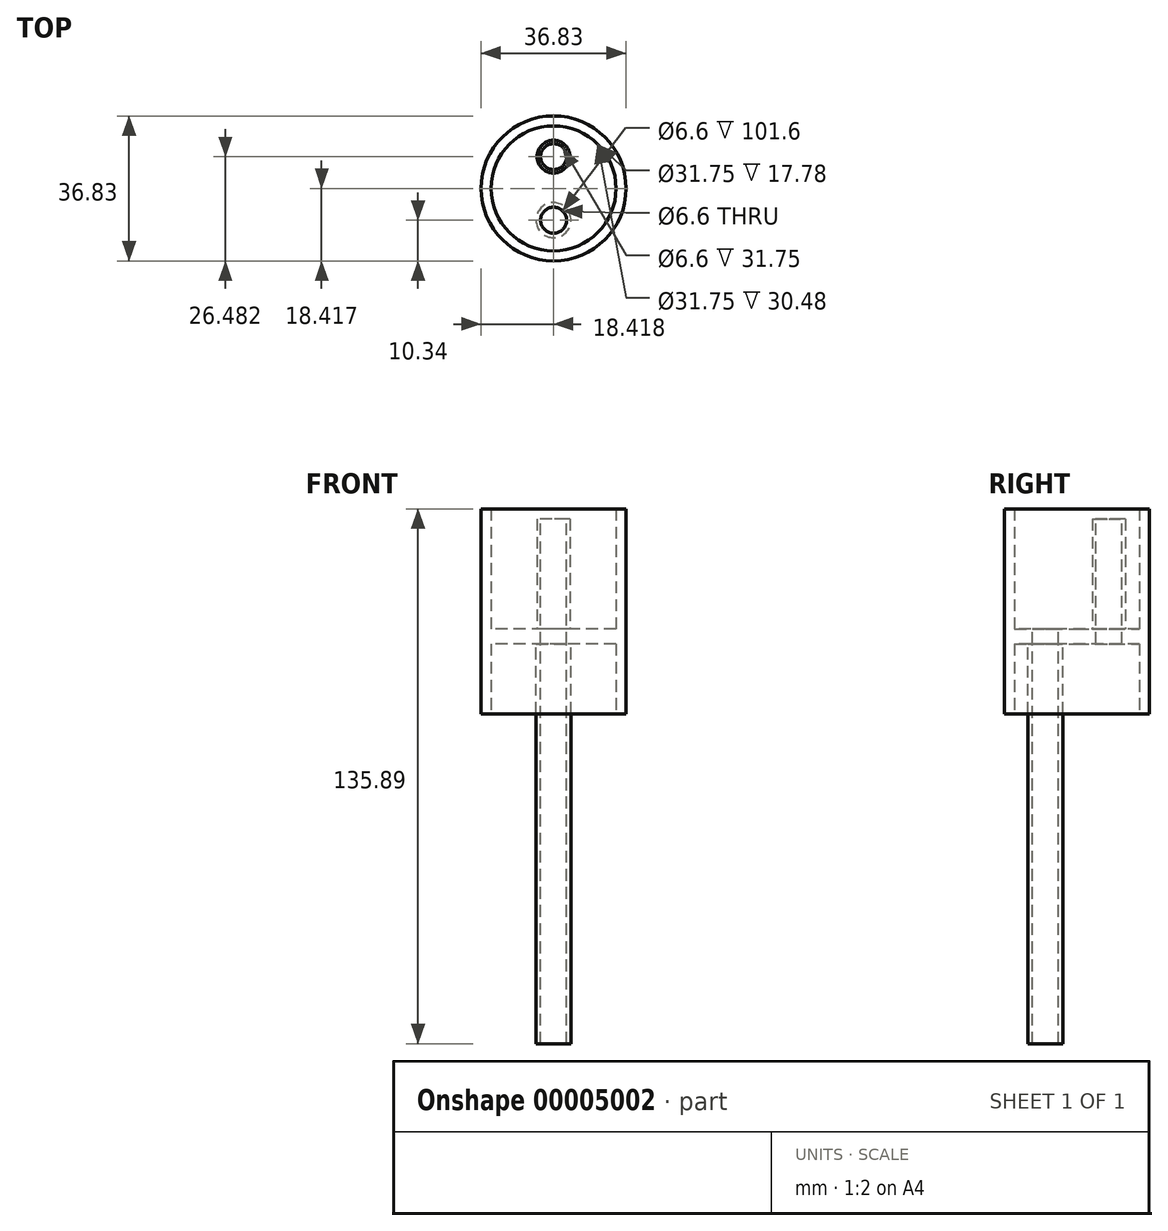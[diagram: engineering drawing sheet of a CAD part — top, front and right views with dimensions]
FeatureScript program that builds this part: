
annotation { "Feature Type Name" : "Feature", "Feature Type Description" : "" }
export const myFeature = defineFeature(function(context is Context, id is Id, definition is map)
    precondition{}
    {
        {
            var Q0;
            Q0=qCreatedBy(makeId("Top.planeOp"),FACE);
            var sketch = newSketch(context, id + "F0", { "sketchPlane" : qUnion([Q0])});
            skCircle(sketch, "E0", {"center": v(-16.23, -12.21) * mm, "radius": 18.41 * mm});
            skCircle(sketch, "E1", {"center": v(-16.23, -12.21) * mm, "radius": 15.88 * mm});
            skSolve(sketch);
        }
        {
            var Q0;
            Q0=makeQuery(id+"F0.imprint","IMPRINT",FACE,{"disambiguationData":[TD([[makeQuery(id+"F0.imprint","IMPRINT",EDGE,{"derivedFrom":sQuery(id+"F0.wireOp",EDGE,"E0")}),1.0]])]});
            extrude(context, id + "F1", {"entities" : qUnion([Q0]), "depth" : 17.78 * mm});
        }
        {
            var Q0;
            Q0=makeQuery(id+"F1.opExtrude","CAP_FACE",FACE,{"disambiguationData":[OSD([sQuery(id+"F0.wireOp",EDGE,"E0"),sQuery(id+"F0.wireOp",EDGE,"E1")])],"isStart":false});
            var sketch = newSketch(context, id + "F2", { "sketchPlane" : qUnion([Q0])});
            skCircle(sketch, "E2", {"center": v(-16.23, -12.21) * mm, "radius": 18.41 * mm});
            skSolve(sketch);
        }
        {
            var Q0;
            Q0 = qSketchRegion(id + "F2", true);
            extrude(context, id + "F3", {"entities" : qUnion([Q0]), "operationType" : NewBodyOperationType.ADD, "depth" : 3.8 * mm});
        }
        {
            var Q0;
            Q0=makeQuery(id+"F3.opExtrude","CAP_FACE",FACE,{"disambiguationData":[OSD([sQuery(id+"F2.wireOp",EDGE,"E2")])],"isStart":false});
            var sketch = newSketch(context, id + "F4", { "sketchPlane" : qUnion([Q0])});
            skLineSegment(sketch, "E3", {"start": v(-16.23, -12.21) * mm, "end": v(-16.23, -7.45) * mm});
            skCircle(sketch, "E4", {"center": v(-16.23, -4.15) * mm, "radius": 3.3 * mm});
            skLineSegment(sketch, "E5", {"start": v(-16.23, -12.21) * mm, "end": v(-16.23, -16.99) * mm});
            skCircle(sketch, "E6", {"center": v(-16.23, -20.29) * mm, "radius": 3.3 * mm});
            skSolve(sketch);
        }
        {
            var Q0;
            Q0=makeQuery(id+"F4.imprint","IMPRINT",FACE,{"disambiguationData":[TD([[makeQuery(id+"F4.imprint","IMPRINT",EDGE,{"derivedFrom":sQuery(id+"F4.wireOp",EDGE,"E4")}),1.0]])]});
            var Q1;
            Q1=makeQuery(id+"F4.imprint","IMPRINT",FACE,{"disambiguationData":[TD([[makeQuery(id+"F4.imprint","IMPRINT",EDGE,{"derivedFrom":sQuery(id+"F4.wireOp",EDGE,"E6")}),1.0]])]});
            extrude(context, id + "F5", {"entities" : qUnion([Q0, Q1]), "operationType" : NewBodyOperationType.REMOVE, "oppositeDirection" : true, "depth" : 3.8 * mm});
        }
        {
            var Q0;
            Q0=makeQuery(id+"F3.opExtrude","CAP_FACE",FACE,{"disambiguationData":[OSD([sQuery(id+"F2.wireOp",EDGE,"E2")])],"isStart":true});
            var sketch = newSketch(context, id + "F6", { "sketchPlane" : qUnion([Q0])});
            skCircle(sketch, "E7", {"center": v(-16.23, 20.29) * mm, "radius": 3.3 * mm});
            skCircle(sketch, "E8", {"center": v(-16.23, 20.29) * mm, "radius": 4.45 * mm});
            skSolve(sketch);
        }
        {
            var Q0;
            Q0=makeQuery(id+"F6.imprint","IMPRINT",FACE,{"disambiguationData":[TD([[makeQuery(id+"F6.imprint","IMPRINT",EDGE,{"derivedFrom":sQuery(id+"F6.wireOp",EDGE,"E7")}),1.0]])]});
            extrude(context, id + "F7", {"entities" : qUnion([Q0]), "depth" : 101.6 * mm});
        }
        {
            var Q0;
            Q0=makeQuery(id+"F3.opExtrude","CAP_FACE",FACE,{"disambiguationData":[OSD([sQuery(id+"F2.wireOp",EDGE,"E2")])],"isStart":false});
            var sketch = newSketch(context, id + "F8", { "sketchPlane" : qUnion([Q0])});
            skCircle(sketch, "E9", {"center": v(-16.23, -4.15) * mm, "radius": 3.3 * mm});
            skCircle(sketch, "E10", {"center": v(-16.23, -4.15) * mm, "radius": 4.2 * mm});
            skSolve(sketch);
        }
        {
            var Q0;
            Q0=makeQuery(id+"F8.imprint","IMPRINT",FACE,{"disambiguationData":[TD([[makeQuery(id+"F8.imprint","IMPRINT",EDGE,{"derivedFrom":sQuery(id+"F8.wireOp",EDGE,"E9")}),-1.0]])]});
            extrude(context, id + "F9", {"entities" : qUnion([Q0]), "operationType" : NewBodyOperationType.ADD, "depth" : 27.94 * mm});
        }
        {
            var Q0;
            Q0=makeQuery(id+"F3.opExtrude","CAP_FACE",FACE,{"disambiguationData":[OSD([sQuery(id+"F2.wireOp",EDGE,"E2")])],"isStart":false});
            var sketch = newSketch(context, id + "F10", { "sketchPlane" : qUnion([Q0])});
            skCircle(sketch, "E11", {"center": v(-16.23, -12.21) * mm, "radius": 18.41 * mm});
            skCircle(sketch, "E12", {"center": v(-16.23, -12.21) * mm, "radius": 15.88 * mm});
            skSolve(sketch);
        }
        {
            var Q0;
            Q0=makeQuery(id+"F10.imprint","IMPRINT",FACE,{"disambiguationData":[TD([[makeQuery(id+"F10.imprint","IMPRINT",EDGE,{"derivedFrom":sQuery(id+"F10.wireOp",EDGE,"E11")}),1.0]])]});
            extrude(context, id + "F11", {"entities" : qUnion([Q0]), "operationType" : NewBodyOperationType.ADD, "depth" : 30.48 * mm});
        }
    });
